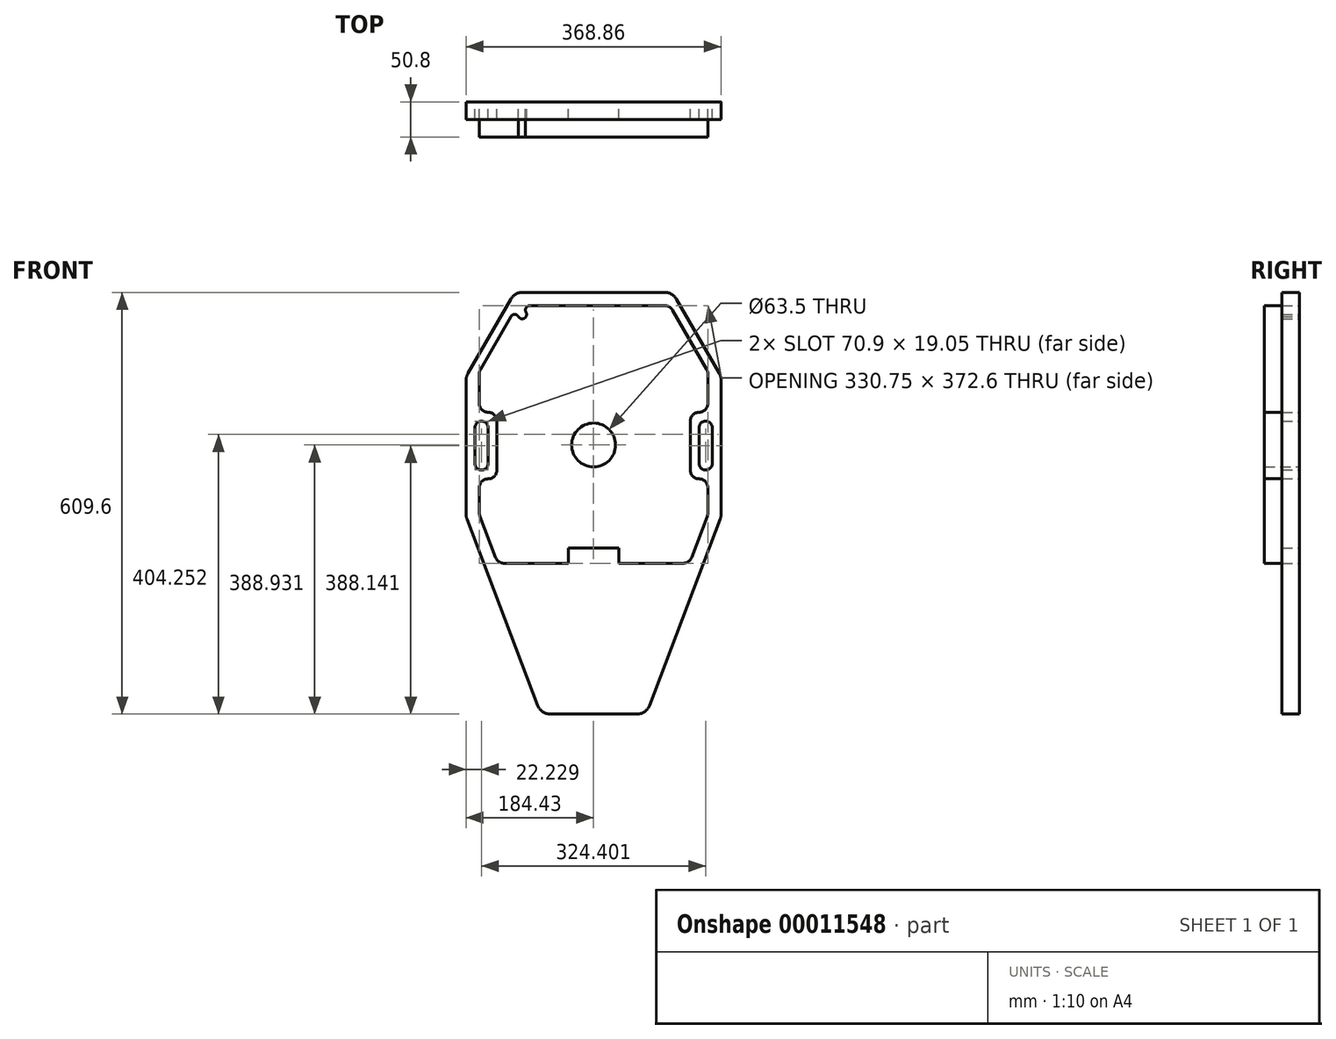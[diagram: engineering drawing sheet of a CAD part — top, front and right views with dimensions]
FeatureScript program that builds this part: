
annotation { "Feature Type Name" : "Feature", "Feature Type Description" : "" }
export const myFeature = defineFeature(function(context is Context, id is Id, definition is map)
    precondition{}
    {
        {
            var Q0;
            Q0=qCreatedBy(makeId("Front.planeOp"),FACE);
            var sketch = newSketch(context, id + "F0", { "sketchPlane" : qUnion([Q0])});
            skLineSegment(sketch, "E0", {"start": v(119.8, 262.07) * mm, "end": v(181.87, 154.55) * mm});
            skLineSegment(sketch, "E1", {"start": v(184.43, 145.03) * mm, "end": v(184.43, -49.57) * mm});
            skLineSegment(sketch, "E2", {"start": v(183.18, -56.34) * mm, "end": v(80.87, -325.72) * mm});
            skLineSegment(sketch, "E3.0.MirrorCS", {"start": v(-184.43, 145.03) * mm, "end": v(-184.43, -49.57) * mm});
            skLineSegment(sketch, "E3.2.MirrorCS", {"start": v(-183.18, -56.34) * mm, "end": v(-80.87, -325.72) * mm});
            skLineSegment(sketch, "E3.4.MirrorCS", {"start": v(-119.8, 262.07) * mm, "end": v(-181.87, 154.55) * mm});
            skLineSegment(sketch, "E4", {"start": v(-103.3, 271.6) * mm, "end": v(103.3, 271.6) * mm});
            skLineSegment(sketch, "E5", {"start": v(-63.06, -338) * mm, "end": v(63.06, -338) * mm});
            skCircle(sketch, "E6", {"center": v(0, 50.92) * mm, "radius": 31.75 * mm});
            skLineSegment(sketch, "E7", {"start": v(103.3, 252.54) * mm, "end": v(0, 252.54) * mm});
            skLineSegment(sketch, "E8", {"start": v(114.3, 246.2) * mm, "end": v(163.67, 160.67) * mm});
            skLineSegment(sketch, "E9", {"start": v(165.38, 154.32) * mm, "end": v(165.38, 110.98) * mm});
            skLineSegment(sketch, "E10", {"start": v(152.68, 98.28) * mm, "end": v(152.68, 98.28) * mm});
            skLineSegment(sketch, "E11", {"start": v(139.98, 85.58) * mm, "end": v(139.98, 14.68) * mm});
            skLineSegment(sketch, "E12", {"start": v(152.68, 1.98) * mm, "end": v(152.68, 1.98) * mm});
            skLineSegment(sketch, "E13", {"start": v(165.38, -10.72) * mm, "end": v(165.38, -47.24) * mm});
            skLineSegment(sketch, "E14", {"start": v(164.55, -51.75) * mm, "end": v(141.72, -111.87) * mm});
            skLineSegment(sketch, "E15", {"start": v(129.84, -120.06) * mm, "end": v(36.38, -120.06) * mm});
            skLineSegment(sketch, "E16", {"start": v(36.38, -120.06) * mm, "end": v(36.38, -98.2) * mm});
            skLineSegment(sketch, "E17", {"start": v(36.38, -98.2) * mm, "end": v(0, -98.2) * mm});
            skPoint(sketch, "E18.visualSharp", {"position": v(138.6, -120.06) * mm});
            skArc(sketch, "E18.filletArc", {"start": v(129.84, -120.06) * mm, "mid": v(137.05, -117.81) * mm, "end": v(141.72, -111.87) * mm});
            skLineSegment(sketch, "E19.bottom", {"start": v(162.2, 85.58) * mm, "end": v(162.2, 85.58) * mm});
            skLineSegment(sketch, "E19.top", {"start": v(162.2, 14.68) * mm, "end": v(162.2, 14.68) * mm});
            skLineSegment(sketch, "E19.left", {"start": v(171.73, 76.06) * mm, "end": v(171.73, 24.2) * mm});
            skLineSegment(sketch, "E19.right", {"start": v(152.68, 76.06) * mm, "end": v(152.68, 24.2) * mm});
            skPoint(sketch, "E20.visualSharp", {"position": v(165.38, 1.98) * mm});
            skArc(sketch, "E20.filletArc", {"start": v(165.38, -10.72) * mm, "mid": v(161.66, -1.74) * mm, "end": v(152.68, 1.98) * mm});
            skPoint(sketch, "E21.visualSharp", {"position": v(139.98, 1.98) * mm});
            skArc(sketch, "E21.filletArc", {"start": v(139.98, 14.68) * mm, "mid": v(143.7, 5.7) * mm, "end": v(152.68, 1.98) * mm});
            skPoint(sketch, "E22.visualSharp", {"position": v(139.98, 98.28) * mm});
            skArc(sketch, "E22.filletArc", {"start": v(152.68, 98.28) * mm, "mid": v(143.7, 94.56) * mm, "end": v(139.98, 85.58) * mm});
            skPoint(sketch, "E23.visualSharp", {"position": v(165.38, 98.28) * mm});
            skArc(sketch, "E23.filletArc", {"start": v(152.68, 98.28) * mm, "mid": v(161.66, 102) * mm, "end": v(165.38, 110.98) * mm});
            skPoint(sketch, "E24.visualSharp", {"position": v(165.38, 157.73) * mm});
            skArc(sketch, "E24.filletArc", {"start": v(165.38, 154.32) * mm, "mid": v(164.94, 157.61) * mm, "end": v(163.67, 160.67) * mm});
            skPoint(sketch, "E25.visualSharp", {"position": v(165.38, -49.57) * mm});
            skArc(sketch, "E25.filletArc", {"start": v(164.55, -51.75) * mm, "mid": v(165.17, -49.54) * mm, "end": v(165.38, -47.24) * mm});
            skPoint(sketch, "E26.visualSharp", {"position": v(110.63, 252.54) * mm});
            skArc(sketch, "E26.filletArc", {"start": v(114.3, 246.2) * mm, "mid": v(109.65, 250.84) * mm, "end": v(103.3, 252.54) * mm});
            skPoint(sketch, "E27.visualSharp", {"position": v(114.3, 271.6) * mm});
            skArc(sketch, "E27.filletArc", {"start": v(119.8, 262.07) * mm, "mid": v(112.83, 269.04) * mm, "end": v(103.3, 271.6) * mm});
            skPoint(sketch, "E28.visualSharp", {"position": v(184.43, 150.13) * mm});
            skArc(sketch, "E28.filletArc", {"start": v(184.43, 145.03) * mm, "mid": v(183.78, 149.96) * mm, "end": v(181.87, 154.55) * mm});
            skPoint(sketch, "E29.visualSharp", {"position": v(184.43, -53.07) * mm});
            skArc(sketch, "E29.filletArc", {"start": v(183.18, -56.34) * mm, "mid": v(184.11, -53.01) * mm, "end": v(184.43, -49.57) * mm});
            skPoint(sketch, "E30.visualSharp", {"position": v(76.2, -338) * mm});
            skArc(sketch, "E30.filletArc", {"start": v(63.06, -338) * mm, "mid": v(73.88, -334.64) * mm, "end": v(80.87, -325.72) * mm});
            skPoint(sketch, "E31.visualSharp", {"position": v(-76.2, -338) * mm});
            skArc(sketch, "E31.filletArc", {"start": v(-80.87, -325.72) * mm, "mid": v(-73.88, -334.64) * mm, "end": v(-63.06, -338) * mm});
            skPoint(sketch, "E32.visualSharp", {"position": v(-184.43, -53.07) * mm});
            skArc(sketch, "E32.filletArc", {"start": v(-184.43, -49.57) * mm, "mid": v(-184.11, -53.01) * mm, "end": v(-183.18, -56.34) * mm});
            skPoint(sketch, "E33.visualSharp", {"position": v(-184.43, 150.13) * mm});
            skArc(sketch, "E33.filletArc", {"start": v(-181.87, 154.55) * mm, "mid": v(-183.78, 149.96) * mm, "end": v(-184.43, 145.03) * mm});
            skPoint(sketch, "E34.visualSharp", {"position": v(-114.3, 271.6) * mm});
            skArc(sketch, "E34.filletArc", {"start": v(-103.3, 271.6) * mm, "mid": v(-112.83, 269.04) * mm, "end": v(-119.8, 262.07) * mm});
            skPoint(sketch, "E35.visualSharp", {"position": v(171.73, 85.58) * mm});
            skArc(sketch, "E35.filletArc", {"start": v(171.73, 76.06) * mm, "mid": v(168.94, 82.8) * mm, "end": v(162.2, 85.58) * mm});
            skPoint(sketch, "E36.visualSharp", {"position": v(171.73, 14.68) * mm});
            skArc(sketch, "E36.filletArc", {"start": v(162.2, 14.68) * mm, "mid": v(168.94, 17.47) * mm, "end": v(171.73, 24.2) * mm});
            skArc(sketch, "E37.filletArc", {"start": v(162.2, 85.58) * mm, "mid": v(155.47, 82.8) * mm, "end": v(152.68, 76.06) * mm});
            skArc(sketch, "E38.filletArc", {"start": v(152.68, 24.2) * mm, "mid": v(155.47, 17.47) * mm, "end": v(162.2, 14.68) * mm});
            skLineSegment(sketch, "E39", {"start": v(0, 0) * mm, "end": v(0, -53.7) * mm});
            skLineSegment(sketch, "E40.0.MirrorCS", {"start": v(-92.3, 252.54) * mm, "end": v(0, 252.54) * mm});
            skLineSegment(sketch, "E41.0.MirrorCS", {"start": v(-114.3, 246.2) * mm, "end": v(-114.3, 246.2) * mm});
            skLineSegment(sketch, "E42.0.MirrorCS", {"start": v(-119.8, 236.67) * mm, "end": v(-163.67, 160.67) * mm});
            skArc(sketch, "E43.0.MirrorCS", {"start": v(-165.38, 154.32) * mm, "mid": v(-164.94, 157.61) * mm, "end": v(-163.67, 160.67) * mm});
            skLineSegment(sketch, "E44.0.MirrorCS", {"start": v(-165.38, 154.32) * mm, "end": v(-165.38, 110.98) * mm});
            skArc(sketch, "E45.0.MirrorCS", {"start": v(-152.68, 98.28) * mm, "mid": v(-161.66, 102) * mm, "end": v(-165.38, 110.98) * mm});
            skArc(sketch, "E46.0.MirrorCS", {"start": v(-152.68, 98.28) * mm, "mid": v(-143.7, 94.56) * mm, "end": v(-139.98, 85.58) * mm});
            skArc(sketch, "E47.0.MirrorCS", {"start": v(-171.73, 76.06) * mm, "mid": v(-168.94, 82.8) * mm, "end": v(-162.2, 85.58) * mm});
            skArc(sketch, "E48.0.MirrorCS", {"start": v(-162.2, 85.58) * mm, "mid": v(-155.47, 82.8) * mm, "end": v(-152.68, 76.06) * mm});
            skLineSegment(sketch, "E49.0.MirrorCS", {"start": v(-139.98, 85.58) * mm, "end": v(-139.98, 14.68) * mm});
            skLineSegment(sketch, "E50.0.MirrorCS", {"start": v(-171.73, 76.06) * mm, "end": v(-171.73, 24.2) * mm});
            skLineSegment(sketch, "E51.0.MirrorCS", {"start": v(-152.68, 76.06) * mm, "end": v(-152.68, 24.2) * mm});
            skArc(sketch, "E52.0.MirrorCS", {"start": v(-162.2, 14.68) * mm, "mid": v(-168.94, 17.47) * mm, "end": v(-171.73, 24.2) * mm});
            skArc(sketch, "E53.0.MirrorCS", {"start": v(-152.68, 24.2) * mm, "mid": v(-155.47, 17.47) * mm, "end": v(-162.2, 14.68) * mm});
            skArc(sketch, "E54.0.MirrorCS", {"start": v(-139.98, 14.68) * mm, "mid": v(-143.7, 5.7) * mm, "end": v(-152.68, 1.98) * mm});
            skArc(sketch, "E55.0.MirrorCS", {"start": v(-165.38, -10.72) * mm, "mid": v(-161.66, -1.74) * mm, "end": v(-152.68, 1.98) * mm});
            skLineSegment(sketch, "E56.0.MirrorCS", {"start": v(-165.38, -10.72) * mm, "end": v(-165.38, -47.24) * mm});
            skArc(sketch, "E57.0.MirrorCS", {"start": v(-164.55, -51.75) * mm, "mid": v(-165.17, -49.54) * mm, "end": v(-165.38, -47.24) * mm});
            skLineSegment(sketch, "E58.0.MirrorCS", {"start": v(-164.55, -51.75) * mm, "end": v(-141.72, -111.87) * mm});
            skArc(sketch, "E59.0.MirrorCS", {"start": v(-129.84, -120.06) * mm, "mid": v(-137.05, -117.81) * mm, "end": v(-141.72, -111.87) * mm});
            skLineSegment(sketch, "E60.0.MirrorCS", {"start": v(-129.84, -120.06) * mm, "end": v(-36.38, -120.06) * mm});
            skLineSegment(sketch, "E61.0.MirrorCS", {"start": v(-36.38, -98.2) * mm, "end": v(0, -98.2) * mm});
            skLineSegment(sketch, "E62.0.MirrorCS", {"start": v(-36.38, -120.06) * mm, "end": v(-36.38, -98.2) * mm});
            skArc(sketch, "E63", {"start": v(-108.87, 236.8) * mm, "mid": v(-100.19, 234.3) * mm, "end": v(-97.8, 243.02) * mm});
            skLineSegment(sketch, "E64", {"start": v(-108.73, 236.54) * mm, "end": v(-108.8, 236.67) * mm});
            skLineSegment(sketch, "E65", {"start": v(-97.8, 243.02) * mm, "end": v(-97.8, 243.02) * mm});
            skPoint(sketch, "E66.visualSharp", {"position": v(-114.3, 246.2) * mm});
            skArc(sketch, "E66.filletArc", {"start": v(-108.8, 236.67) * mm, "mid": v(-114.3, 239.84) * mm, "end": v(-119.8, 236.67) * mm});
            skArc(sketch, "E67.filletArc", {"start": v(-92.3, 252.54) * mm, "mid": v(-97.8, 249.37) * mm, "end": v(-97.8, 243.02) * mm});
            skSolve(sketch);
        }
        {
            var Q0;
            Q0=makeQuery(id+"F0.imprint","IMPRINT",FACE,{"disambiguationData":[TD([[makeQuery(id+"F0.imprint","IMPRINT",EDGE,{"derivedFrom":sQuery(id+"F0.wireOp",EDGE,"E6")}),-1.0]])]});
            extrude(context, id + "F1", {"entities" : qUnion([Q0]), "depth" : 50.8 * mm});
        }
        {
            var Q0;
            Q0 = qSketchRegion(id + "F0", true);
            extrude(context, id + "F2", {"entities" : qUnion([Q0]), "depth" : 25.4 * mm});
        }
    });
